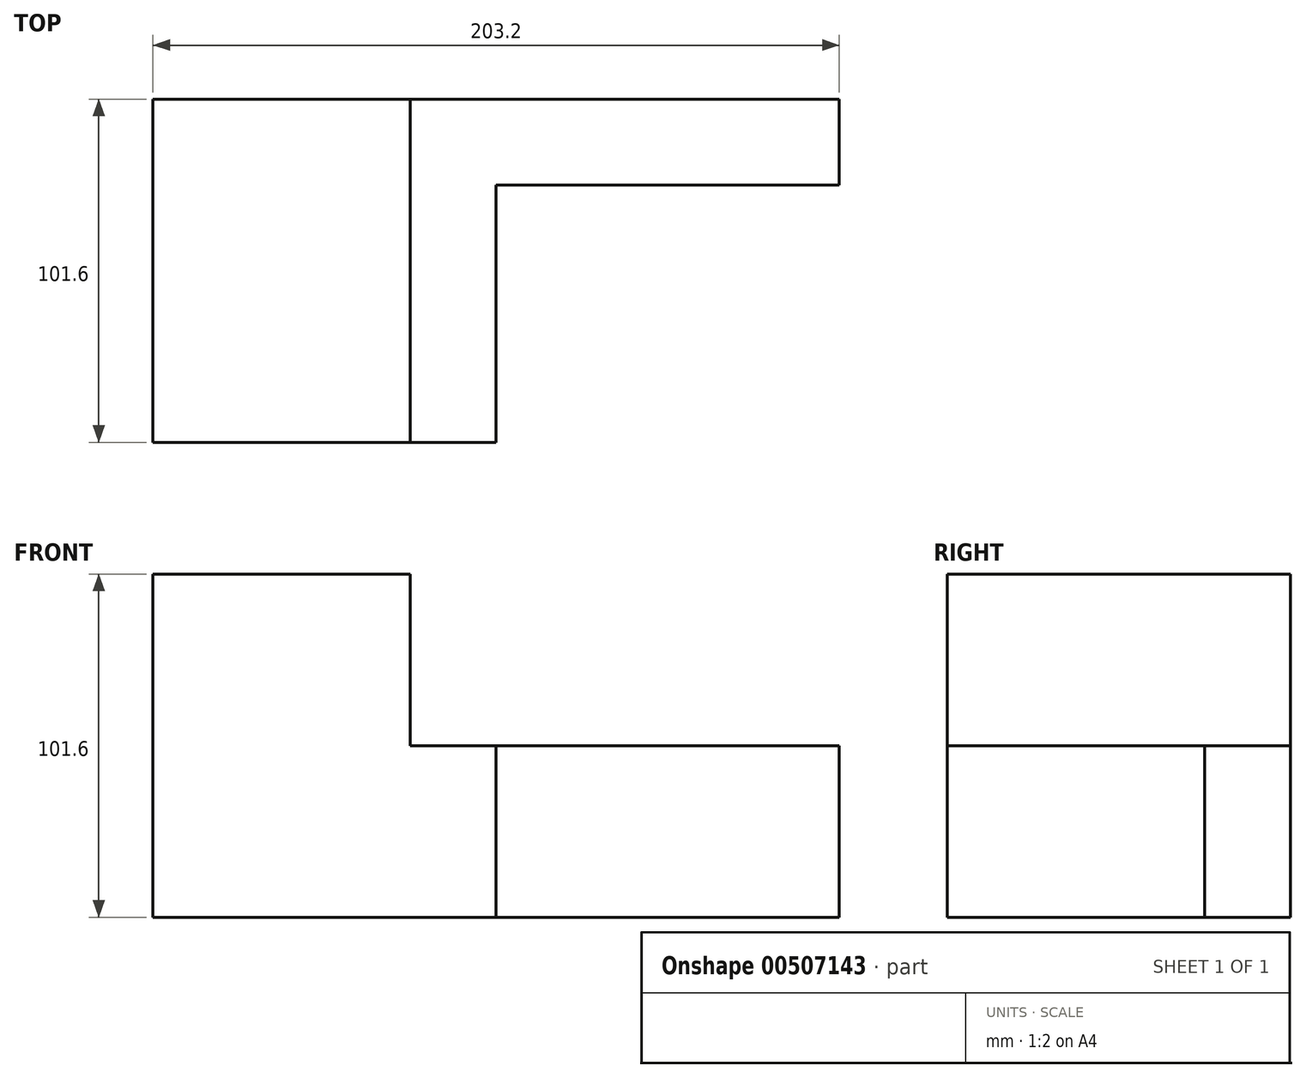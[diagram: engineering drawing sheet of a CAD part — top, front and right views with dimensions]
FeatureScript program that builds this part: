
annotation { "Feature Type Name" : "Feature", "Feature Type Description" : "" }
export const myFeature = defineFeature(function(context is Context, id is Id, definition is map)
    precondition{}
    {
        {
            var Q0;
            Q0=qCreatedBy(makeId("Front.planeOp"),FACE);
            var sketch = newSketch(context, id + "F0", { "sketchPlane" : qUnion([Q0])});
            skLineSegment(sketch, "E0.bottom", {"start": v(0, 0) * mm, "end": v(-127, 0) * mm});
            skLineSegment(sketch, "E0.top", {"start": v(0, 50.8) * mm, "end": v(-127, 50.8) * mm});
            skLineSegment(sketch, "E0.left", {"start": v(0, 0) * mm, "end": v(0, 50.8) * mm});
            skLineSegment(sketch, "E0.right", {"start": v(-127, 0) * mm, "end": v(-127, 50.8) * mm});
            skLineSegment(sketch, "E1.bottom", {"start": v(-127, 0) * mm, "end": v(-203.2, 0) * mm});
            skLineSegment(sketch, "E1.top", {"start": v(-127, 101.6) * mm, "end": v(-203.2, 101.6) * mm});
            skLineSegment(sketch, "E1.left", {"start": v(-127, 0) * mm, "end": v(-127, 101.6) * mm});
            skLineSegment(sketch, "E1.right", {"start": v(-203.2, 0) * mm, "end": v(-203.2, 101.6) * mm});
            skSolve(sketch);
        }
        {
            var Q0;
            Q0 = qSketchRegion(id + "F0", true);
            var Q1;
            {var subQ3=sQuery(id+"F0.wireOp",EDGE,"E1.bottom");Q1=makeQuery(id+"F0.imprint","IMPRINT",FACE,{"disambiguationData":[TD([[makeQuery(id+"F0.imprint","IMPRINT",EDGE,{"derivedFrom":subQ3}),-1.0]])]});}
            var Q2;
            {var subQ0=sQuery(id+"F0.wireOp",EDGE,"E0.bottom");Q2=makeQuery(id+"F0.imprint","IMPRINT",FACE,{"disambiguationData":[TD([[makeQuery(id+"F0.imprint","IMPRINT",EDGE,{"derivedFrom":subQ0}),-1.0]])]});}
            extrude(context, id + "F1", {"entities" : qUnion([Q0, Q1, Q2]), "depth" : 101.6 * mm});
        }
        {
            var Q0;
            Q0=makeQuery(id+"F1.opExtrude","SWEPT_FACE",FACE,{"disambiguationData":[OSD([sQuery(id+"F0.wireOp",EDGE,"E0.left")])]});
            var sketch = newSketch(context, id + "F2", { "sketchPlane" : qUnion([Q0])});
            skLineSegment(sketch, "E2.bottom", {"start": v(-25.4, 0) * mm, "end": v(-101.6, 0) * mm});
            skLineSegment(sketch, "E2.top", {"start": v(-25.4, 50.8) * mm, "end": v(-101.6, 50.8) * mm});
            skLineSegment(sketch, "E2.left", {"start": v(-25.4, 0) * mm, "end": v(-25.4, 50.8) * mm});
            skLineSegment(sketch, "E2.right", {"start": v(-101.6, 0) * mm, "end": v(-101.6, 50.8) * mm});
            skSolve(sketch);
        }
        {
            var Q0;
            Q0=makeQuery(id+"F2.imprint","IMPRINT",FACE,{"disambiguationData":[TD([[makeQuery(id+"F2.imprint","IMPRINT",EDGE,{"derivedFrom":sQuery(id+"F2.wireOp",EDGE,"E2.bottom")}),1.0]])]});
            extrude(context, id + "F3", {"entities" : qUnion([Q0]), "operationType" : NewBodyOperationType.REMOVE, "oppositeDirection" : true, "depth" : 101.6 * mm});
        }
    });
